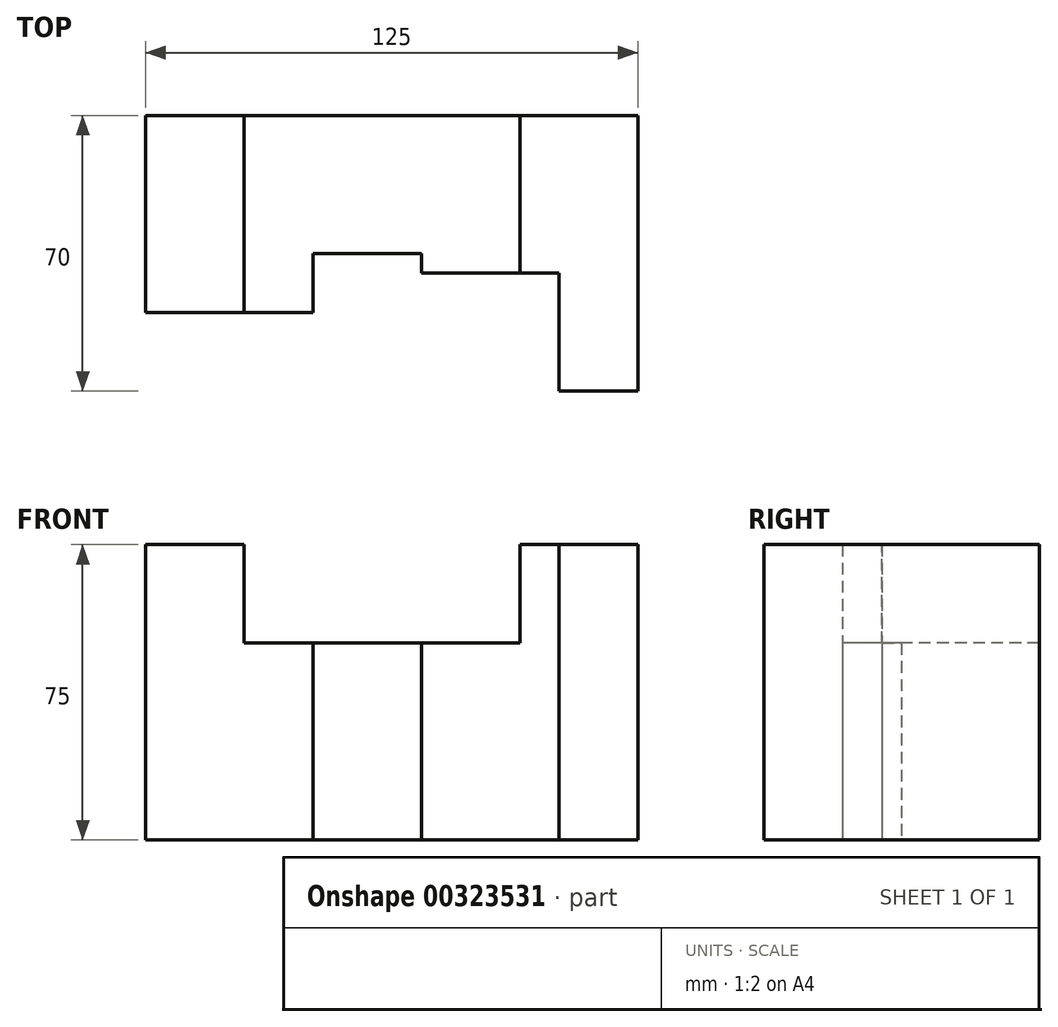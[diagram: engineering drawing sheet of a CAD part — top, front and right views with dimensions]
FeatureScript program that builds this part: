
annotation { "Feature Type Name" : "Feature", "Feature Type Description" : "" }
export const myFeature = defineFeature(function(context is Context, id is Id, definition is map)
    precondition{}
    {
        {
            var Q0;
            Q0=qCreatedBy(makeId("Top.planeOp"),FACE);
            var sketch = newSketch(context, id + "F0", { "sketchPlane" : qUnion([Q0])});
            skLineSegment(sketch, "E0.bottom", {"start": v(0, 0) * mm, "end": v(25, 0) * mm});
            skLineSegment(sketch, "E0.top", {"start": v(0, 50) * mm, "end": v(25, 50) * mm});
            skLineSegment(sketch, "E0.left", {"start": v(0, 0) * mm, "end": v(0, 50) * mm});
            skLineSegment(sketch, "E0.right", {"start": v(25, 0) * mm, "end": v(25, 50) * mm});
            skLineSegment(sketch, "E1.bottom", {"start": v(25, 0) * mm, "end": v(42.5, 0) * mm});
            skLineSegment(sketch, "E1.top", {"start": v(25, 50) * mm, "end": v(42.5, 50) * mm});
            skLineSegment(sketch, "E1.right", {"start": v(42.5, 0) * mm, "end": v(42.5, 50) * mm});
            skLineSegment(sketch, "E2.bottom", {"start": v(42.5, 50) * mm, "end": v(70, 50) * mm});
            skLineSegment(sketch, "E2.top", {"start": v(42.5, 15) * mm, "end": v(70, 15) * mm});
            skLineSegment(sketch, "E2.left", {"start": v(42.5, 50) * mm, "end": v(42.5, 15) * mm});
            skLineSegment(sketch, "E2.right", {"start": v(70, 50) * mm, "end": v(70, 15) * mm});
            skLineSegment(sketch, "E3.bottom", {"start": v(70, 50) * mm, "end": v(95, 50) * mm});
            skLineSegment(sketch, "E3.top", {"start": v(70, 10) * mm, "end": v(95, 10) * mm});
            skLineSegment(sketch, "E3.left", {"start": v(70, 50) * mm, "end": v(70, 10) * mm});
            skLineSegment(sketch, "E3.right", {"start": v(95, 50) * mm, "end": v(95, 10) * mm});
            skLineSegment(sketch, "E4.bottom", {"start": v(95, 50) * mm, "end": v(105, 50) * mm});
            skLineSegment(sketch, "E4.top", {"start": v(95, 10) * mm, "end": v(105, 10) * mm});
            skLineSegment(sketch, "E4.right", {"start": v(105, 50) * mm, "end": v(105, 10) * mm});
            skLineSegment(sketch, "E5.bottom", {"start": v(105, 50) * mm, "end": v(125, 50) * mm});
            skLineSegment(sketch, "E5.top", {"start": v(105, -20) * mm, "end": v(125, -20) * mm});
            skLineSegment(sketch, "E5.left", {"start": v(105, 50) * mm, "end": v(105, -20) * mm});
            skLineSegment(sketch, "E5.right", {"start": v(125, 50) * mm, "end": v(125, -20) * mm});
            skSolve(sketch);
        }
        {
            var Q0;
            Q0 = qSketchRegion(id + "F0", true);
            extrude(context, id + "F1", {"entities" : qUnion([Q0]), "depth" : 75 * mm});
        }
        {
            var Q0;
            Q0=qCreatedBy(makeId("Front.planeOp"),FACE);
            var sketch = newSketch(context, id + "F2", { "sketchPlane" : qUnion([Q0])});
            skLineSegment(sketch, "E6.bottom", {"start": v(25, 75) * mm, "end": v(95, 75) * mm});
            skLineSegment(sketch, "E6.top", {"start": v(25, 50) * mm, "end": v(95, 50) * mm});
            skLineSegment(sketch, "E6.left", {"start": v(25, 75) * mm, "end": v(25, 50) * mm});
            skLineSegment(sketch, "E6.right", {"start": v(95, 75) * mm, "end": v(95, 50) * mm});
            skSolve(sketch);
        }
        {
            var Q0;
            Q0 = qSketchRegion(id + "F2", true);
            extrude(context, id + "F3", {"entities" : qUnion([Q0]), "operationType" : NewBodyOperationType.REMOVE, "endBound" : BoundingType.THROUGH_ALL, "oppositeDirection" : true, "depth" : 25 * mm});
        }
    });
